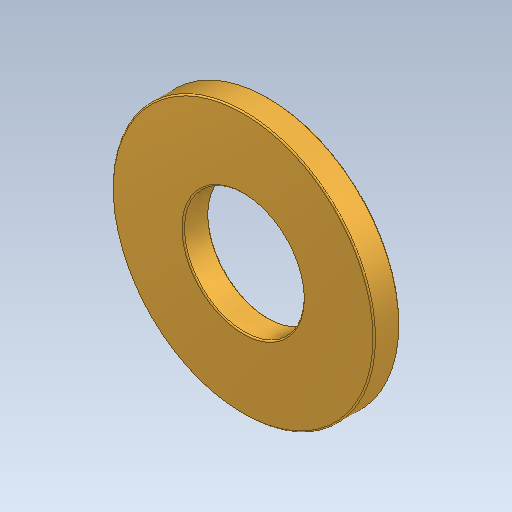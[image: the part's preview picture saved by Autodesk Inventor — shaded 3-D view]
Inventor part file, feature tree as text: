
AUTODESK INVENTOR PART (.ipt)
format: ipt  version: 2023 (Build 270158000, 158)  size: 126,464 bytes
history: native  units: in
note: dims shown in document units (in); Inventor stores cm internally (conversion verified against a paired STEP export)
features: fillet x1
ambient origin geometry x8: Origin, YZ Plane, XZ Plane, XY Plane, X Axis, Y Axis, Z Axis, Center Point
bodies: Solid1 (feature_tree)
feature tree (1):
  fillet  "Fillet1"  [1 undecoded]
note: 1 required parameter value undecoded (feature->parameter linkage not recoverable at this tier; creation-order binding heuristic only, values carry confidence <= 0.55)
